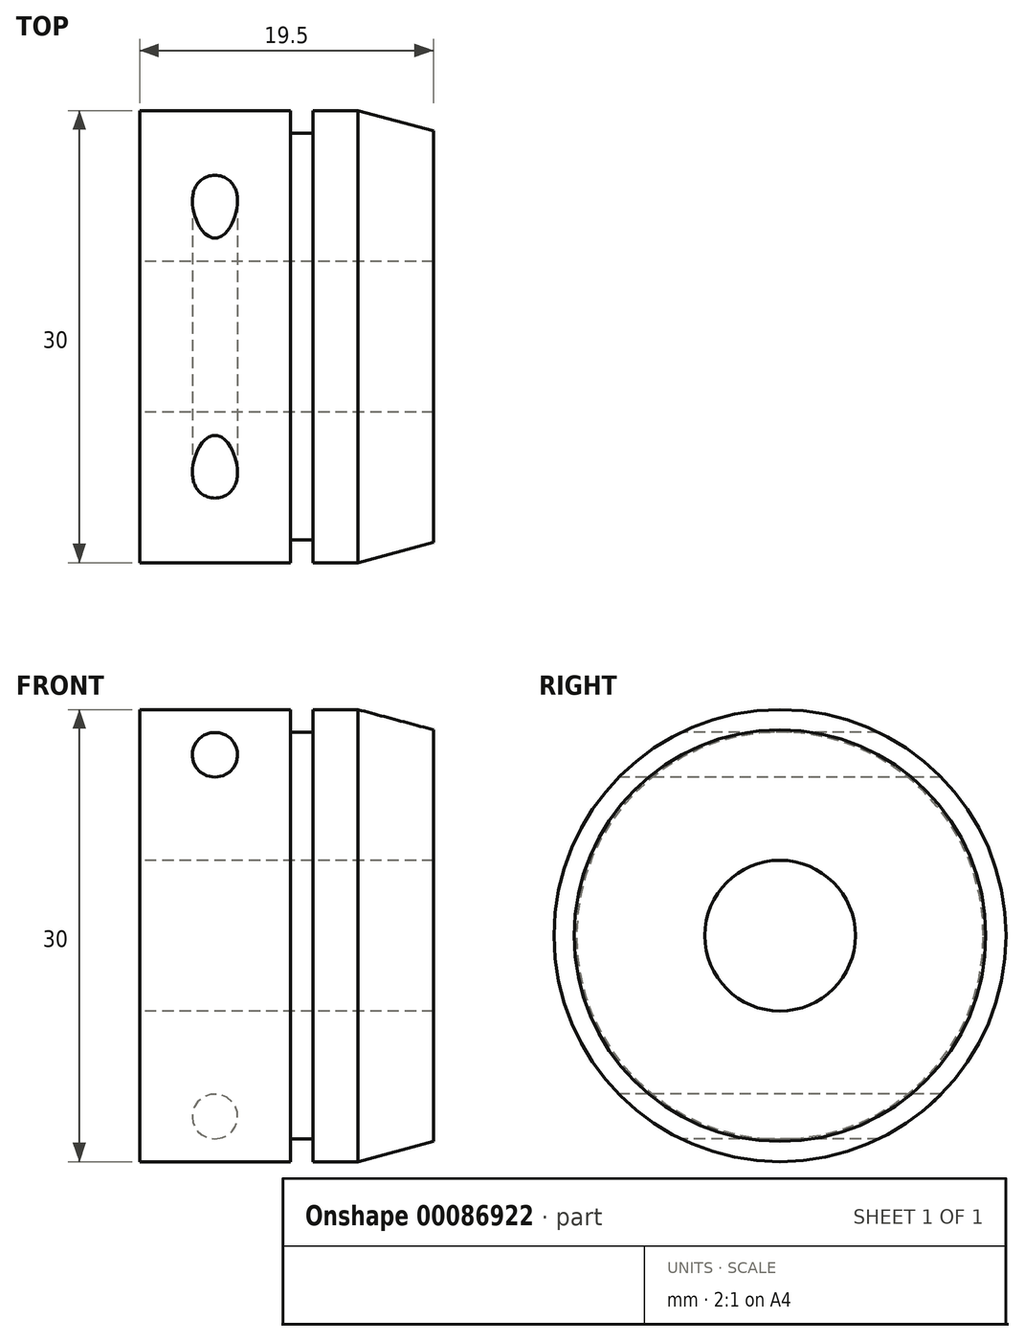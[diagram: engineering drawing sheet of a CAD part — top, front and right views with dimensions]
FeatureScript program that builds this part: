
annotation { "Feature Type Name" : "Feature", "Feature Type Description" : "" }
export const myFeature = defineFeature(function(context is Context, id is Id, definition is map)
    precondition{}
    {
        {
            var Q0;
            Q0=qCreatedBy(makeId("Front.planeOp"),FACE);
            var sketch = newSketch(context, id + "F0", { "sketchPlane" : qUnion([Q0])});
            skLineSegment(sketch, "E0", {"start": v(19.5, 0) * mm, "end": v(19.5, 13.66) * mm});
            skLineSegment(sketch, "E1", {"start": v(19.5, 13.66) * mm, "end": v(14.5, 15) * mm});
            skLineSegment(sketch, "E2", {"start": v(14.5, 15) * mm, "end": v(11.5, 15) * mm});
            skLineSegment(sketch, "E3", {"start": v(0, 15) * mm, "end": v(0, 5) * mm});
            skLineSegment(sketch, "E4", {"start": v(10, 15) * mm, "end": v(10, 13.5) * mm});
            skLineSegment(sketch, "E5", {"start": v(10, 13.5) * mm, "end": v(11.5, 13.5) * mm});
            skLineSegment(sketch, "E6", {"start": v(11.5, 13.5) * mm, "end": v(11.5, 15) * mm});
            skLineSegment(sketch, "E7.trimOffspring", {"start": v(10, 15) * mm, "end": v(0, 15) * mm});
            skLineSegment(sketch, "E8", {"start": v(0, 5) * mm, "end": v(0, 0) * mm, "construction": true});
            skLineSegment(sketch, "E9", {"start": v(0, 0) * mm, "end": v(19.5, 0) * mm, "construction": true});
            skLineSegment(sketch, "E10", {"start": v(19.5, 0) * mm, "end": v(19.5, 0) * mm});
            skLineSegment(sketch, "E11", {"start": v(0, 5) * mm, "end": v(19.5, 5) * mm});
            skSolve(sketch);
        }
        {
            var Q0;
            {var subQ0=sQuery(id+"F0.wireOp",EDGE,"E1");Q0=makeQuery(id+"F0.imprint","IMPRINT",FACE,{"disambiguationData":[TD([[makeQuery(id+"F0.imprint","IMPRINT",EDGE,{"derivedFrom":subQ0}),1.0]])]});}
            var Q1;
            Q1=sQuery(id+"F0.wireOp",EDGE,"E9");
            revolve(context, id + "F1", {"entities" : qUnion([Q0]), "axis" : qUnion([Q1]), "revolveType" : RevolveType.FULL});
        }
        {
            var Q0;
            Q0=qCreatedBy(makeId("Front.planeOp"),FACE);
            var sketch = newSketch(context, id + "F2", { "sketchPlane" : qUnion([Q0])});
            skCircle(sketch, "E12", {"center": v(5, 12) * mm, "radius": 1.5 * mm});
            skCircle(sketch, "E13", {"center": v(5, -12) * mm, "radius": 1.5 * mm});
            skLineSegment(sketch, "E14", {"start": v(5, -12) * mm, "end": v(5, 12) * mm, "construction": true});
            skLineSegment(sketch, "E15", {"start": v(5, 0) * mm, "end": v(0, 0) * mm});
            skLineSegment(sketch, "E16", {"start": v(5, 13.5) * mm, "end": v(0, 13.5) * mm, "construction": true});
            skLineSegment(sketch, "E17", {"start": v(0, 13.5) * mm, "end": v(0, 0) * mm, "construction": true});
            skPoint(sketch, "E18", {"position": v(0, 15) * mm});
            skSolve(sketch);
        }
        {
            var Q0;
            Q0 = qSketchRegion(id + "F2", true);
            extrude(context, id + "F3", {"entities" : qUnion([Q0]), "operationType" : NewBodyOperationType.REMOVE, "endBound" : BoundingType.THROUGH_ALL, "oppositeDirection" : true, "depth" : 25 * mm, "hasSecondDirection" : true, "secondDirectionBound" : SecondDirectionBoundingType.THROUGH_ALL, "secondDirectionOppositeDirection" : false, "secondDirectionDepth" : 25 * mm});
        }
    });
